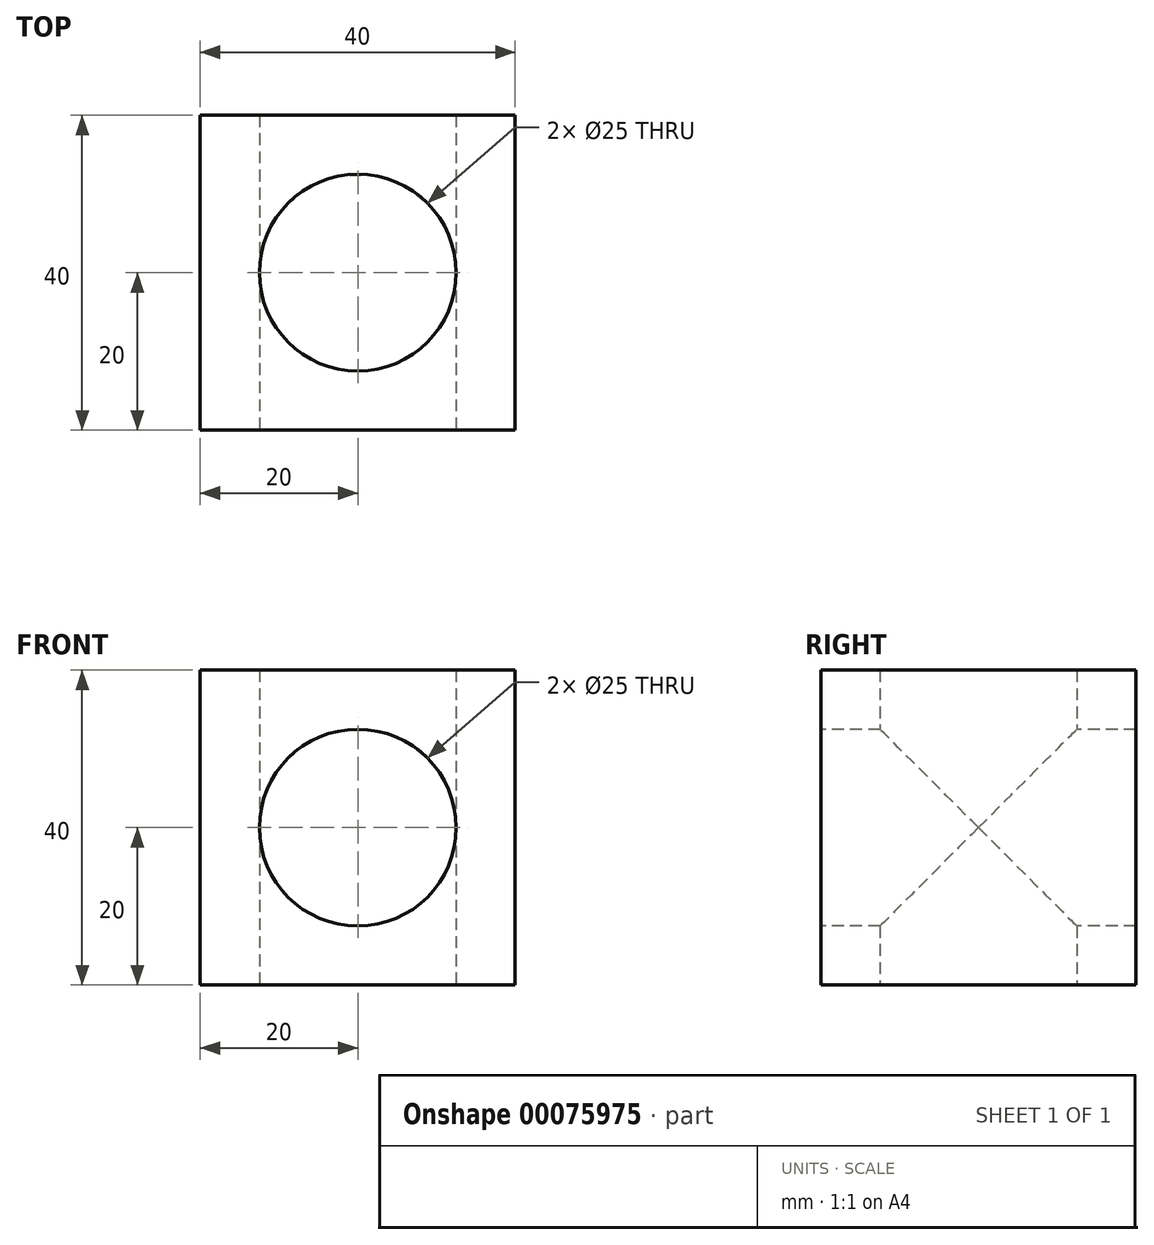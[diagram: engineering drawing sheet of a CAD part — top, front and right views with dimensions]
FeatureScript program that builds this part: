
annotation { "Feature Type Name" : "Feature", "Feature Type Description" : "" }
export const myFeature = defineFeature(function(context is Context, id is Id, definition is map)
    precondition{}
    {
        {
            var Q0;
            Q0=qCreatedBy(makeId("Top.planeOp"),FACE);
            var sketch = newSketch(context, id + "F0", { "sketchPlane" : qUnion([Q0])});
            skLineSegment(sketch, "E0.bottom", {"start": v(20, -20) * mm, "end": v(-20, -20) * mm});
            skLineSegment(sketch, "E0.top", {"start": v(20, 20) * mm, "end": v(-20, 20) * mm});
            skLineSegment(sketch, "E0.left", {"start": v(20, -20) * mm, "end": v(20, 20) * mm});
            skLineSegment(sketch, "E0.right", {"start": v(-20, -20) * mm, "end": v(-20, 20) * mm});
            skPoint(sketch, "E0.middle", {"position": v(0, 0) * mm});
            skCircle(sketch, "E1", {"center": v(0, 0) * mm, "radius": 12.5 * mm});
            skSolve(sketch);
        }
        {
            var Q0;
            Q0=makeQuery(id+"F0.imprint","IMPRINT",FACE,{"disambiguationData":[TD([[makeQuery(id+"F0.imprint","IMPRINT",EDGE,{"derivedFrom":sQuery(id+"F0.wireOp",EDGE,"E0.bottom")}),-1.0]])]});
            extrude(context, id + "F1", {"entities" : qUnion([Q0]), "depth" : 40 * mm});
        }
        {
            var Q0;
            Q0=makeQuery(id+"F1.opExtrude","SWEPT_FACE",FACE,{"disambiguationData":[OSD([sQuery(id+"F0.wireOp",EDGE,"E0.bottom")])]});
            var sketch = newSketch(context, id + "F2", { "sketchPlane" : qUnion([Q0])});
            skLineSegment(sketch, "E2", {"start": v(0, 0) * mm, "end": v(0, 40) * mm, "construction": true});
            skLineSegment(sketch, "E3", {"start": v(-20, 20) * mm, "end": v(20, 20) * mm, "construction": true});
            skCircle(sketch, "E4", {"center": v(0, 20) * mm, "radius": 12.5 * mm});
            skSolve(sketch);
        }
        {
            var Q0;
            Q0=makeQuery(id+"F2.imprint","IMPRINT",FACE,{"disambiguationData":[TD([[makeQuery(id+"F2.imprint","IMPRINT",EDGE,{"derivedFrom":sQuery(id+"F2.wireOp",EDGE,"E4")}),1.0]])]});
            extrude(context, id + "F3", {"entities" : qUnion([Q0]), "operationType" : NewBodyOperationType.REMOVE, "endBound" : BoundingType.THROUGH_ALL, "oppositeDirection" : true, "depth" : 25 * mm});
        }
    });
